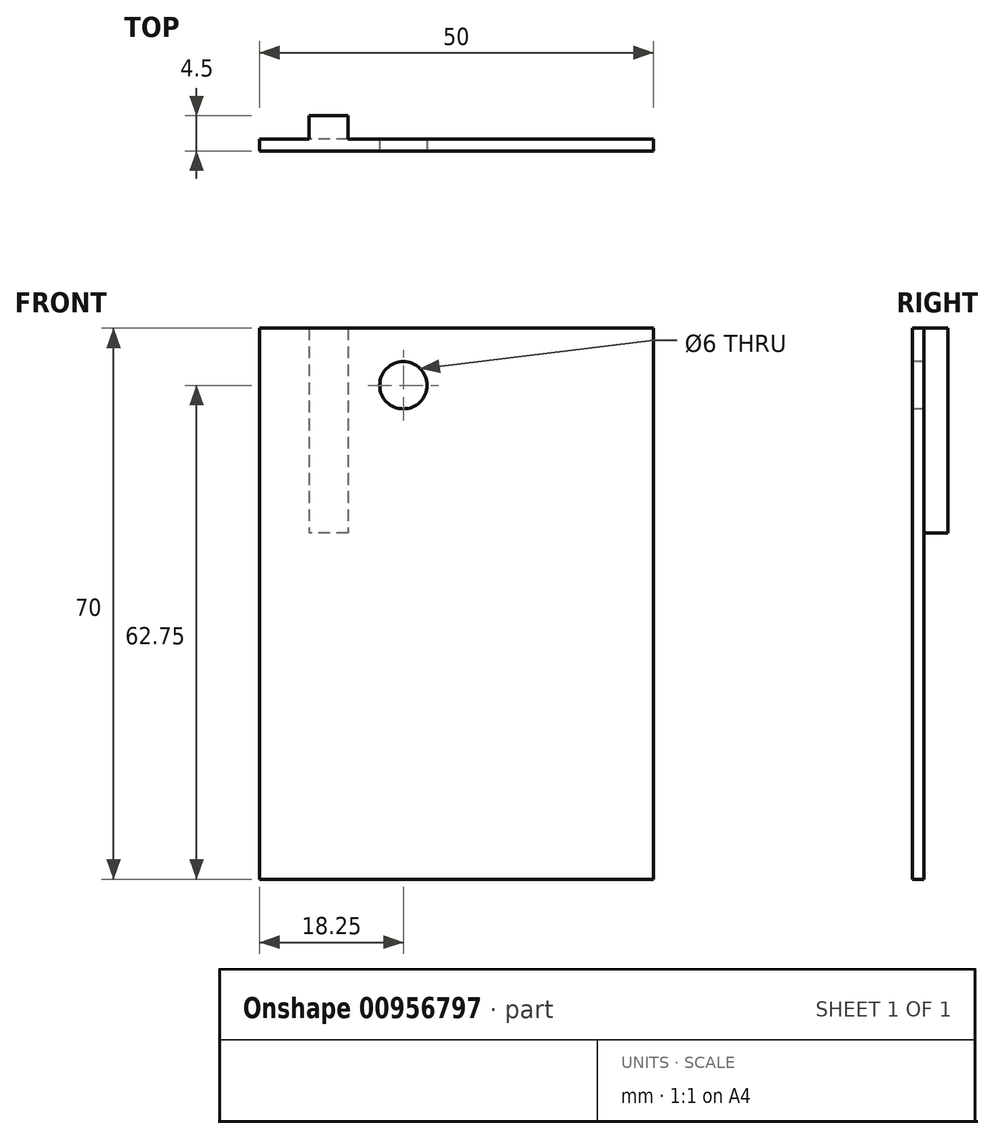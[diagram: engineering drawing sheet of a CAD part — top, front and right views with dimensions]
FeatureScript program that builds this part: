
annotation { "Feature Type Name" : "Feature", "Feature Type Description" : "" }
export const myFeature = defineFeature(function(context is Context, id is Id, definition is map)
    precondition{}
    {
        {
            var Q0;
            Q0=qCreatedBy(makeId("Front.planeOp"),FACE);
            var sketch = newSketch(context, id + "F0", { "sketchPlane" : qUnion([Q0])});
            skLineSegment(sketch, "E0.bottom", {"start": v(13, -13) * mm, "end": v(-13, -13) * mm});
            skLineSegment(sketch, "E0.top", {"start": v(13, 13) * mm, "end": v(-13, 13) * mm});
            skLineSegment(sketch, "E0.left", {"start": v(13, -13) * mm, "end": v(13, 13) * mm});
            skLineSegment(sketch, "E0.right", {"start": v(-13, -13) * mm, "end": v(-13, 13) * mm});
            skPoint(sketch, "E0.middle", {"position": v(0, 0) * mm});
            skSolve(sketch);
        }
        {
            var Q0;
            Q0=qSketchRegion(id+"F0",true);
            extrude(context, id + "F1", {"entities" : qUnion([Q0]), "oppositeDirection" : true, "depth" : 1.5 * mm, "offsetDistance" : 25 * mm});
        }
        {
            var Q0;
            Q0=makeQuery(id+"F1.opExtrude","CAP_FACE",FACE,{"disambiguationData":[OSD([sQuery(id+"F0.wireOp",EDGE,"E0.bottom"),sQuery(id+"F0.wireOp",EDGE,"E0.top"),sQuery(id+"F0.wireOp",EDGE,"E0.left"),sQuery(id+"F0.wireOp",EDGE,"E0.right")])],"isStart":false});
            var sketch = newSketch(context, id + "F2", { "sketchPlane" : qUnion([Q0])});
            skLineSegment(sketch, "E1.bottom", {"start": v(6.75, 13) * mm, "end": v(1.75, 13) * mm});
            skLineSegment(sketch, "E1.top", {"start": v(6.75, -13) * mm, "end": v(1.75, -13) * mm});
            skLineSegment(sketch, "E1.left", {"start": v(6.75, 13) * mm, "end": v(6.75, -13) * mm});
            skLineSegment(sketch, "E1.right", {"start": v(1.75, 13) * mm, "end": v(1.75, -13) * mm});
            skSolve(sketch);
        }
        {
            var Q0;
            Q0=qSketchRegion(id+"F2",true);
            extrude(context, id + "F3", {"entities" : qUnion([Q0]), "operationType" : NewBodyOperationType.ADD, "depth" : 3 * mm, "offsetDistance" : 25 * mm});
        }
        {
            var Q0;
            Q0=makeQuery(id+"F1.opExtrude","CAP_FACE",FACE,{"disambiguationData":[OSD([sQuery(id+"F0.wireOp",EDGE,"E0.bottom"),sQuery(id+"F0.wireOp",EDGE,"E0.top"),sQuery(id+"F0.wireOp",EDGE,"E0.left"),sQuery(id+"F0.wireOp",EDGE,"E0.right")])],"isStart":true});
            var sketch = newSketch(context, id + "F4", { "sketchPlane" : qUnion([Q0])});
            skCircle(sketch, "E2", {"center": v(5.25, 5.75) * mm, "radius": 3 * mm});
            skSolve(sketch);
        }
        {
            var Q0;
            Q0=qSketchRegion(id+"F4",true);
            extrude(context, id + "F5", {"entities" : qUnion([Q0]), "operationType" : NewBodyOperationType.REMOVE, "oppositeDirection" : true, "depth" : 25 * mm, "offsetDistance" : 25 * mm});
        }
        {
            var Q0;
            Q0=makeQuery(id+"F1.opExtrude","SWEPT_FACE",FACE,{"disambiguationData":[OSD([sQuery(id+"F0.wireOp",EDGE,"E0.left")])]});
            extrude(context, id + "F6", {"entities" : qUnion([Q0]), "operationType" : NewBodyOperationType.ADD, "depth" : 24 * mm, "offsetDistance" : 25 * mm});
        }
        {
            var Q0;
            {var subQ0=sQuery(id+"F0.wireOp",EDGE,"E0.bottom");Q0=makeQuery(id+"F6.boolean.opBoolean","MERGE",FACE,{"derivedFrom":[makeQuery(id+"F3.boolean.opBoolean","MERGE",FACE,{"derivedFrom":[makeQuery(id+"F1.opExtrude","SWEPT_FACE",FACE,{"disambiguationData":[OSD([subQ0])]}),makeQuery(id+"F3.opExtrude","SWEPT_FACE",FACE,{"disambiguationData":[OSD([sQuery(id+"F2.wireOp",EDGE,"E1.top")])]})]}),makeQuery(id+"F6.opExtrude","SWEPT_FACE",FACE,{"disambiguationData":[OSD([subQ0,sQuery(id+"F0.wireOp",EDGE,"E0.left")])]})]});}
            var sketch = newSketch(context, id + "F7", { "sketchPlane" : qUnion([Q0])});
            skLineSegment(sketch, "E3.bottom", {"start": v(-13, 0) * mm, "end": v(37, 0) * mm});
            skLineSegment(sketch, "E3.top", {"start": v(-13, -1.5) * mm, "end": v(37, -1.5) * mm});
            skLineSegment(sketch, "E3.left", {"start": v(-13, 0) * mm, "end": v(-13, -1.5) * mm});
            skLineSegment(sketch, "E3.right", {"start": v(37, 0) * mm, "end": v(37, -1.5) * mm});
            skSolve(sketch);
        }
        {
            var Q0;
            Q0 = qSketchRegion(id + "F7", true);
            extrude(context, id + "F8", {"entities" : qUnion([Q0]), "operationType" : NewBodyOperationType.ADD, "depth" : 44 * mm, "offsetDistance" : 25 * mm});
        }
    });
